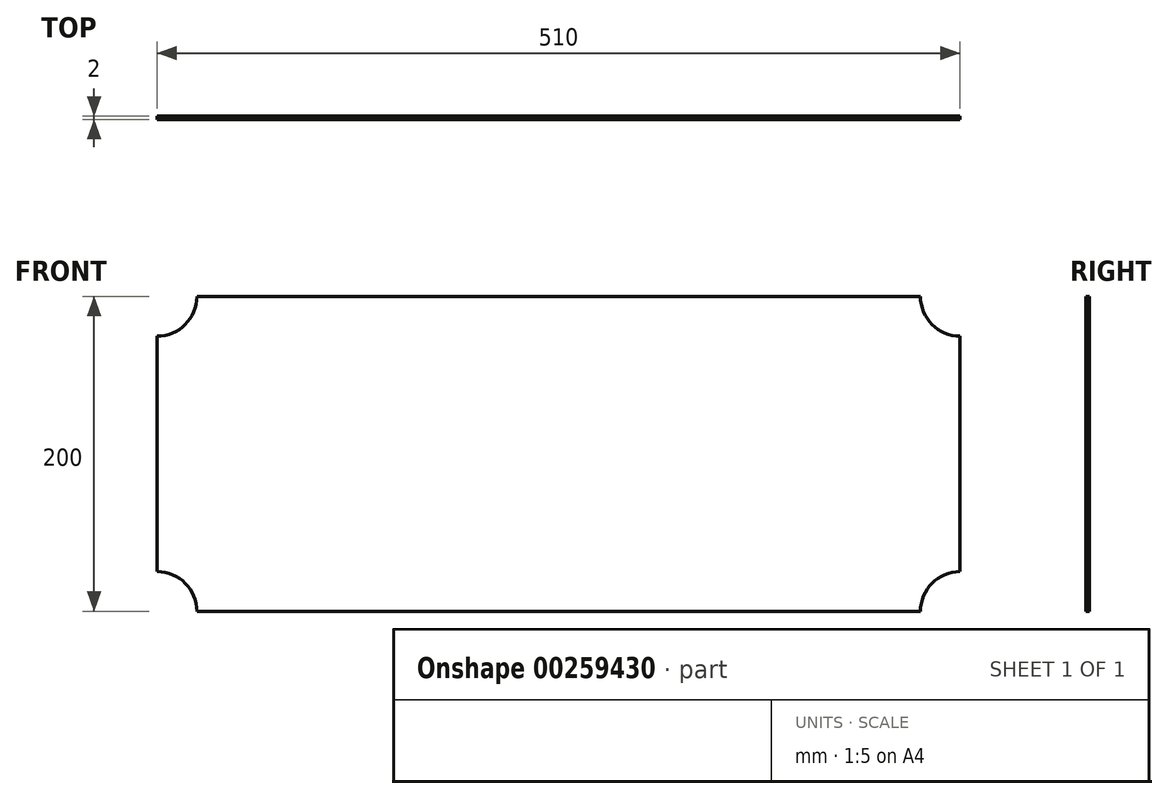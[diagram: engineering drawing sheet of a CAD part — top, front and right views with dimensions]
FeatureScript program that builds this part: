
annotation { "Feature Type Name" : "Feature", "Feature Type Description" : "" }
export const myFeature = defineFeature(function(context is Context, id is Id, definition is map)
    precondition{}
    {
        {
            var Q0;
            Q0=qCreatedBy(makeId("Front.planeOp"),FACE);
            var sketch = newSketch(context, id + "F0", { "sketchPlane" : qUnion([Q0])});
            skLineSegment(sketch, "E0.bottom", {"start": v(-270.88, -70.68) * mm, "end": v(179.12, -70.68) * mm, "construction": true});
            skLineSegment(sketch, "E0.top", {"start": v(-270.88, 129.32) * mm, "end": v(179.12, 129.32) * mm, "construction": true});
            skLineSegment(sketch, "E0.left", {"start": v(-270.88, -70.68) * mm, "end": v(-270.88, -40.68) * mm, "construction": true});
            skLineSegment(sketch, "E0.right", {"start": v(179.12, -70.68) * mm, "end": v(179.12, -40.68) * mm, "construction": true});
            skLineSegment(sketch, "E1", {"start": v(-45.88, 70.98) * mm, "end": v(-45.88, 55.98) * mm, "construction": true});
            skLineSegment(sketch, "E2", {"start": v(-45.88, 55.98) * mm, "end": v(-127.55, 55.98) * mm, "construction": true});
            skLineSegment(sketch, "E3", {"start": v(-300.88, 129.32) * mm, "end": v(-314.7, 129.32) * mm, "construction": true});
            skLineSegment(sketch, "E4", {"start": v(-314.7, 129.32) * mm, "end": v(-314.7, 70.98) * mm, "construction": true});
            skLineSegment(sketch, "E5.MirrorCS", {"start": v(179.12, 129.32) * mm, "end": v(199.12, 129.32) * mm, "construction": true});
            skLineSegment(sketch, "E6.MirrorCS", {"start": v(222.93, 129.32) * mm, "end": v(222.93, 70.98) * mm, "construction": true});
            skLineSegment(sketch, "E7.MirrorCS", {"start": v(-314.7, -17.37) * mm, "end": v(-314.7, 40.98) * mm, "construction": true});
            skLineSegment(sketch, "E8.MirrorCS", {"start": v(222.93, -17.37) * mm, "end": v(222.93, 40.98) * mm, "construction": true});
            skLineSegment(sketch, "E9.MirrorCS", {"start": v(179.12, -17.37) * mm, "end": v(199.48, -17.37) * mm, "construction": true});
            skLineSegment(sketch, "E10.MirrorCS", {"start": v(-270.88, -17.37) * mm, "end": v(-274.47, -17.37) * mm, "construction": true});
            skLineSegment(sketch, "E11", {"start": v(-314.7, 40.98) * mm, "end": v(222.93, 40.98) * mm, "construction": true});
            skLineSegment(sketch, "E12", {"start": v(-290.88, 129.32) * mm, "end": v(-300.88, 129.32) * mm});
            skLineSegment(sketch, "E13", {"start": v(-300.88, 129.32) * mm, "end": v(-300.88, 134.1) * mm});
            skLineSegment(sketch, "E14", {"start": v(-275.65, 159.32) * mm, "end": v(183.9, 159.32) * mm});
            skLineSegment(sketch, "E15", {"start": v(209.12, 134.1) * mm, "end": v(209.12, -15.45) * mm});
            skLineSegment(sketch, "E16", {"start": v(183.9, -40.68) * mm, "end": v(-275.65, -40.68) * mm});
            skLineSegment(sketch, "E17", {"start": v(-300.88, -15.45) * mm, "end": v(-300.88, 129.32) * mm});
            skLineSegment(sketch, "E18.1", {"start": v(-290.88, -17.52) * mm, "end": v(-290.88, -17.37) * mm});
            skLineSegment(sketch, "E18.2", {"start": v(179.12, -30.68) * mm, "end": v(175.34, -30.68) * mm});
            skArc(sketch, "E19", {"start": v(-300.88, 134.1) * mm, "mid": v(-283.04, 141.48) * mm, "end": v(-275.65, 159.32) * mm});
            skArc(sketch, "E20.MirrorCS", {"start": v(199.12, 125.54) * mm, "mid": v(194.76, 127.15) * mm, "end": v(190.65, 129.32) * mm});
            skArc(sketch, "E21.MirrorCS", {"start": v(209.12, 134.1) * mm, "mid": v(191.28, 141.48) * mm, "end": v(183.9, 159.32) * mm});
            skLineSegment(sketch, "E22", {"start": v(-300.88, 59.32) * mm, "end": v(-250.82, 59.32) * mm, "construction": true});
            skPoint(sketch, "E22.endSnap0", {"position": v(-290.88, 59.32) * mm});
            skArc(sketch, "E23.MirrorCS", {"start": v(-300.88, -15.45) * mm, "mid": v(-283.04, -22.84) * mm, "end": v(-275.65, -40.68) * mm});
            skArc(sketch, "E24.MirrorCS", {"start": v(209.12, -15.45) * mm, "mid": v(191.28, -22.84) * mm, "end": v(183.9, -40.68) * mm});
            skPoint(sketch, "E25.orphan", {"position": v(-265.65, -40.68) * mm});
            skPoint(sketch, "E26.orphan", {"position": v(-290.88, -30.68) * mm});
            skPoint(sketch, "E27.orphan", {"position": v(-290.88, 149.32) * mm});
            skPoint(sketch, "E28.orphan", {"position": v(-265.65, 159.32) * mm});
            skPoint(sketch, "E29.orphan", {"position": v(173.9, 159.32) * mm});
            skLineSegment(sketch, "E30.trimOffspring", {"start": v(209.12, 129.32) * mm, "end": v(222.93, 129.32) * mm, "construction": true});
            skPoint(sketch, "E31.orphan", {"position": v(209.12, 124.1) * mm});
            skPoint(sketch, "E32.orphan", {"position": v(173.9, -40.68) * mm});
            skLineSegment(sketch, "E33.trimOffspring", {"start": v(179.12, -30.68) * mm, "end": v(179.12, 129.32) * mm, "construction": true});
            skLineSegment(sketch, "E34.trimOffspring", {"start": v(199.12, -17.37) * mm, "end": v(199.12, -17.52) * mm});
            skPoint(sketch, "E35.orphan", {"position": v(209.12, -5.45) * mm});
            skLineSegment(sketch, "E36.trimOffspring", {"start": v(209.12, -17.37) * mm, "end": v(222.93, -17.37) * mm, "construction": true});
            skPoint(sketch, "E37.0.start.orphan", {"position": v(-300.88, 124.1) * mm});
            skPoint(sketch, "E38.orphan", {"position": v(-300.88, -5.45) * mm});
            skLineSegment(sketch, "E39.trimOffspring", {"start": v(-290.88, -17.37) * mm, "end": v(-314.7, -17.37) * mm, "construction": true});
            skLineSegment(sketch, "E40.trimOffspring", {"start": v(-270.88, -22.2) * mm, "end": v(-270.88, 129.32) * mm, "construction": true});
            skSolve(sketch);
        }
        {
            var Q0;
            Q0 = qSketchRegion(id + "F0", true);
            extrude(context, id + "F1", {"entities" : qUnion([Q0]), "depth" : 2 * mm});
        }
    });
